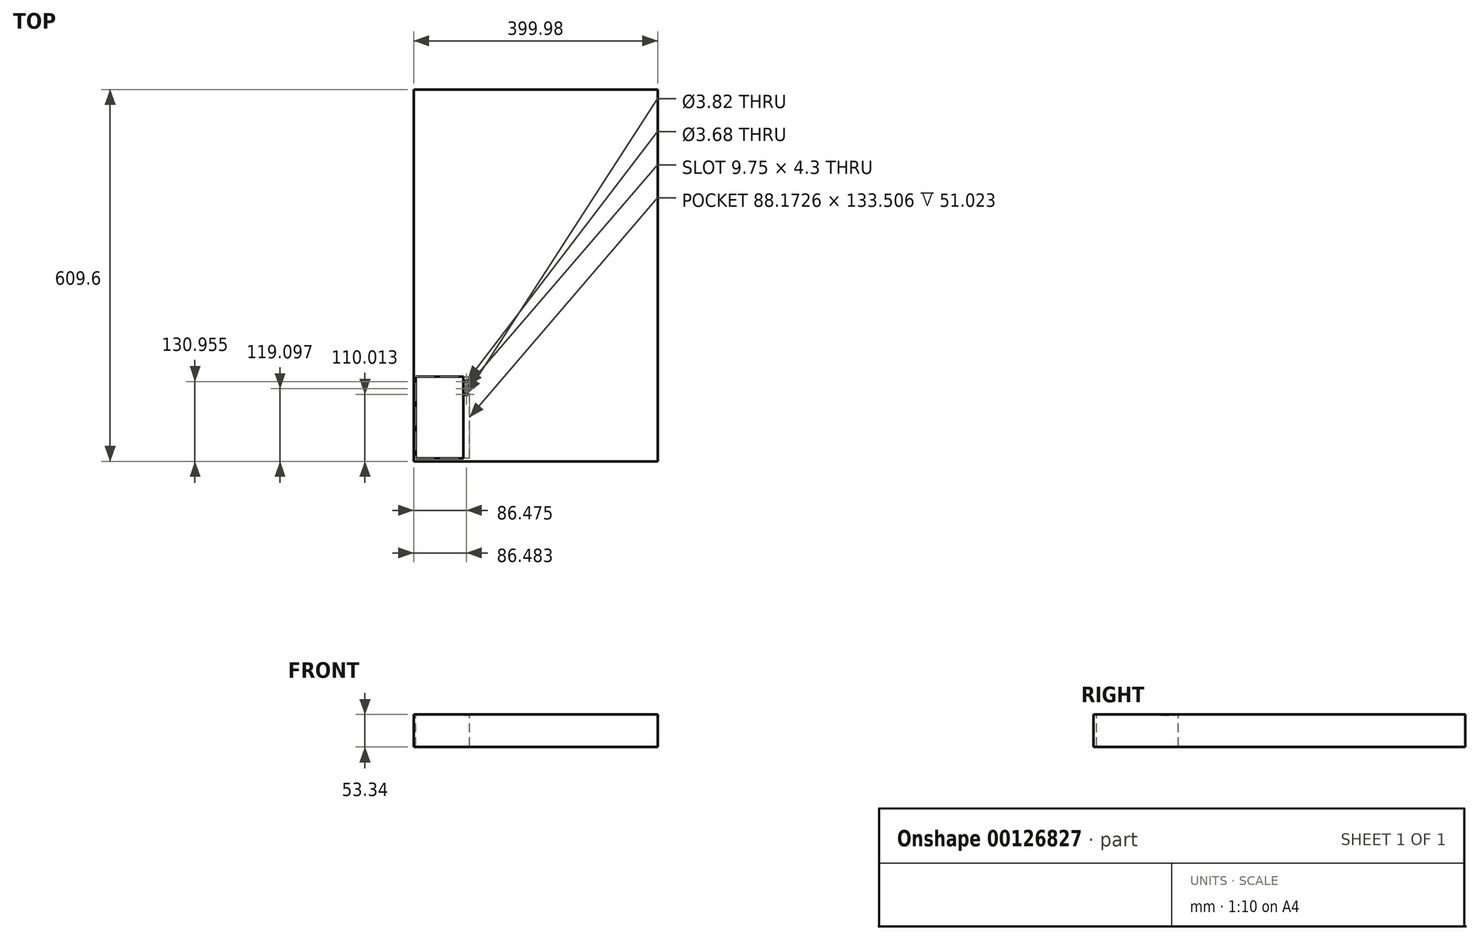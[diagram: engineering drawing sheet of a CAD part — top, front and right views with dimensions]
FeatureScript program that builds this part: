
annotation { "Feature Type Name" : "Feature", "Feature Type Description" : "" }
export const myFeature = defineFeature(function(context is Context, id is Id, definition is map)
    precondition{}
    {
        {
            var Q0;
            Q0=qCreatedBy(makeId("Top.planeOp"),FACE);
            var sketch = newSketch(context, id + "F0", { "sketchPlane" : qUnion([Q0])});
            skLineSegment(sketch, "E0.bottom", {"start": v(0, 0) * mm, "end": v(399.98, 0) * mm});
            skLineSegment(sketch, "E0.top", {"start": v(0, 609.6) * mm, "end": v(399.98, 609.6) * mm});
            skLineSegment(sketch, "E0.left", {"start": v(0, 0) * mm, "end": v(0, 609.6) * mm});
            skLineSegment(sketch, "E0.right", {"start": v(399.98, 0) * mm, "end": v(399.98, 609.6) * mm});
            skSolve(sketch);
        }
        {
            var Q0;
            Q0=makeQuery(id+"F0.imprint","IMPRINT",FACE,{"disambiguationData":[TD([[makeQuery(id+"F0.imprint","IMPRINT",EDGE,{"derivedFrom":sQuery(id+"F0.wireOp",EDGE,"E0.bottom")}),1.0]])]});
            extrude(context, id + "F1", {"entities" : qUnion([Q0]), "depth" : 53.34 * mm});
        }
        {
            var Q0;
            Q0=makeQuery(id+"F1.opExtrude","CAP_FACE",FACE,{"disambiguationData":[OSD([sQuery(id+"F0.wireOp",EDGE,"E0.bottom"),sQuery(id+"F0.wireOp",EDGE,"E0.top"),sQuery(id+"F0.wireOp",EDGE,"E0.left"),sQuery(id+"F0.wireOp",EDGE,"E0.right")])],"isStart":false});
            var sketch = newSketch(context, id + "F2", { "sketchPlane" : qUnion([Q0])});
            skLineSegment(sketch, "E1.bottom", {"start": v(3.37, 5.21) * mm, "end": v(81.38, 5.21) * mm});
            skLineSegment(sketch, "E1.top", {"start": v(3.37, 138.72) * mm, "end": v(81.38, 138.72) * mm});
            skLineSegment(sketch, "E1.left", {"start": v(3.37, 5.21) * mm, "end": v(3.37, 138.72) * mm});
            skLineSegment(sketch, "E1.right", {"start": v(81.38, 5.21) * mm, "end": v(81.38, 138.72) * mm});
            skSolve(sketch);
        }
        {
            var Q0;
            Q0=makeQuery(id+"F2.imprint","IMPRINT",FACE,{"disambiguationData":[TD([[makeQuery(id+"F2.imprint","IMPRINT",EDGE,{"derivedFrom":sQuery(id+"F2.wireOp",EDGE,"E1.bottom")}),1.0]])]});
            extrude(context, id + "F3", {"entities" : qUnion([Q0]), "operationType" : NewBodyOperationType.REMOVE, "oppositeDirection" : true, "depth" : 52.07 * mm});
        }
        {
            var Q0;
            Q0=makeQuery(id+"F3.boolean.opBoolean","COPY",FACE,{"derivedFrom":makeQuery(id+"F3.opExtrude","SWEPT_FACE",FACE,{"disambiguationData":[OSD([sQuery(id+"F2.wireOp",EDGE,"E1.right")])]})});
            var sketch = newSketch(context, id + "F4", { "sketchPlane" : qUnion([Q0])});
            skLineSegment(sketch, "E2", {"start": v(-138.72, 52.3) * mm, "end": v(-5.21, 52.3) * mm});
            skSolve(sketch);
        }
        {
            var Q0;
            {var subQ0=sQuery(id+"F4.wireOp",EDGE,"E2");Q0=makeQuery(id+"F4.imprint","IMPRINT",FACE,{"disambiguationData":[TD([[makeQuery(id+"F4.imprint","IMPRINT",EDGE,{"derivedFrom":subQ0}),-1.0]])]});}
            extrude(context, id + "F5", {"entities" : qUnion([Q0]), "operationType" : NewBodyOperationType.REMOVE, "oppositeDirection" : true, "depth" : 10.16 * mm});
        }
        {
            var Q0;
            Q0=makeQuery(id+"F1.opExtrude","CAP_FACE",FACE,{"disambiguationData":[OSD([sQuery(id+"F0.wireOp",EDGE,"E0.bottom"),sQuery(id+"F0.wireOp",EDGE,"E0.top"),sQuery(id+"F0.wireOp",EDGE,"E0.left"),sQuery(id+"F0.wireOp",EDGE,"E0.right")])],"isStart":false});
            var sketch = newSketch(context, id + "F6", { "sketchPlane" : qUnion([Q0])});
            skLineSegment(sketch, "E3", {"start": v(86.48, 133.94) * mm, "end": v(86.48, 121.89) * mm, "construction": true});
            skCircle(sketch, "E4", {"center": v(86.48, 130.95) * mm, "radius": 1.84 * mm});
            skCircle(sketch, "E5", {"center": v(86.48, 110.01) * mm, "radius": 1.91 * mm});
            skArc(sketch, "E6", {"start": v(84.42, 117.02) * mm, "mid": v(86.16, 114.22) * mm, "end": v(88.63, 116.4) * mm});
            skArc(sketch, "E7", {"start": v(88.57, 121.91) * mm, "mid": v(86.26, 123.97) * mm, "end": v(84.42, 121.48) * mm});
            skLineSegment(sketch, "E8", {"start": v(88.63, 116.36) * mm, "end": v(88.57, 121.91) * mm});
            skLineSegment(sketch, "E9", {"start": v(84.42, 122.3) * mm, "end": v(84.42, 117.02) * mm});
            skLineSegment(sketch, "E10.trimOffspring", {"start": v(86.48, 116.36) * mm, "end": v(86.48, 107.72) * mm, "construction": true});
            skSolve(sketch);
        }
        {
            var Q0;
            Q0=makeQuery(id+"F6.imprint","IMPRINT",FACE,{"disambiguationData":[TD([[makeQuery(id+"F6.imprint","IMPRINT",EDGE,{"derivedFrom":sQuery(id+"F6.wireOp",EDGE,"E4")}),1.0]])]});
            var Q1;
            {var subQ1=sQuery(id+"F6.wireOp",EDGE,"E6");var subQ5=sQuery(id+"F6.wireOp",EDGE,"E9");var subQ6=makeQuery(id+"F6.imprint","INTERSECT",VERTEX,{"derivedFrom":[subQ1,subQ5]});Q1=makeQuery(id+"F6.imprint","IMPRINT",FACE,{"disambiguationData":[TD([[makeQuery(id+"F6.imprint","IMPRINT",EDGE,{"disambiguationData":[TD([[subQ6,-1.0]])],"derivedFrom":subQ1}),1.0]])]});}
            var Q2;
            Q2=makeQuery(id+"F6.imprint","IMPRINT",FACE,{"disambiguationData":[TD([[makeQuery(id+"F6.imprint","IMPRINT",EDGE,{"derivedFrom":sQuery(id+"F6.wireOp",EDGE,"E5")}),1.0]])]});
            extrude(context, id + "F7", {"entities" : qUnion([Q0, Q1, Q2]), "operationType" : NewBodyOperationType.REMOVE, "oppositeDirection" : true, "depth" : 25.4 * mm});
        }
    });
